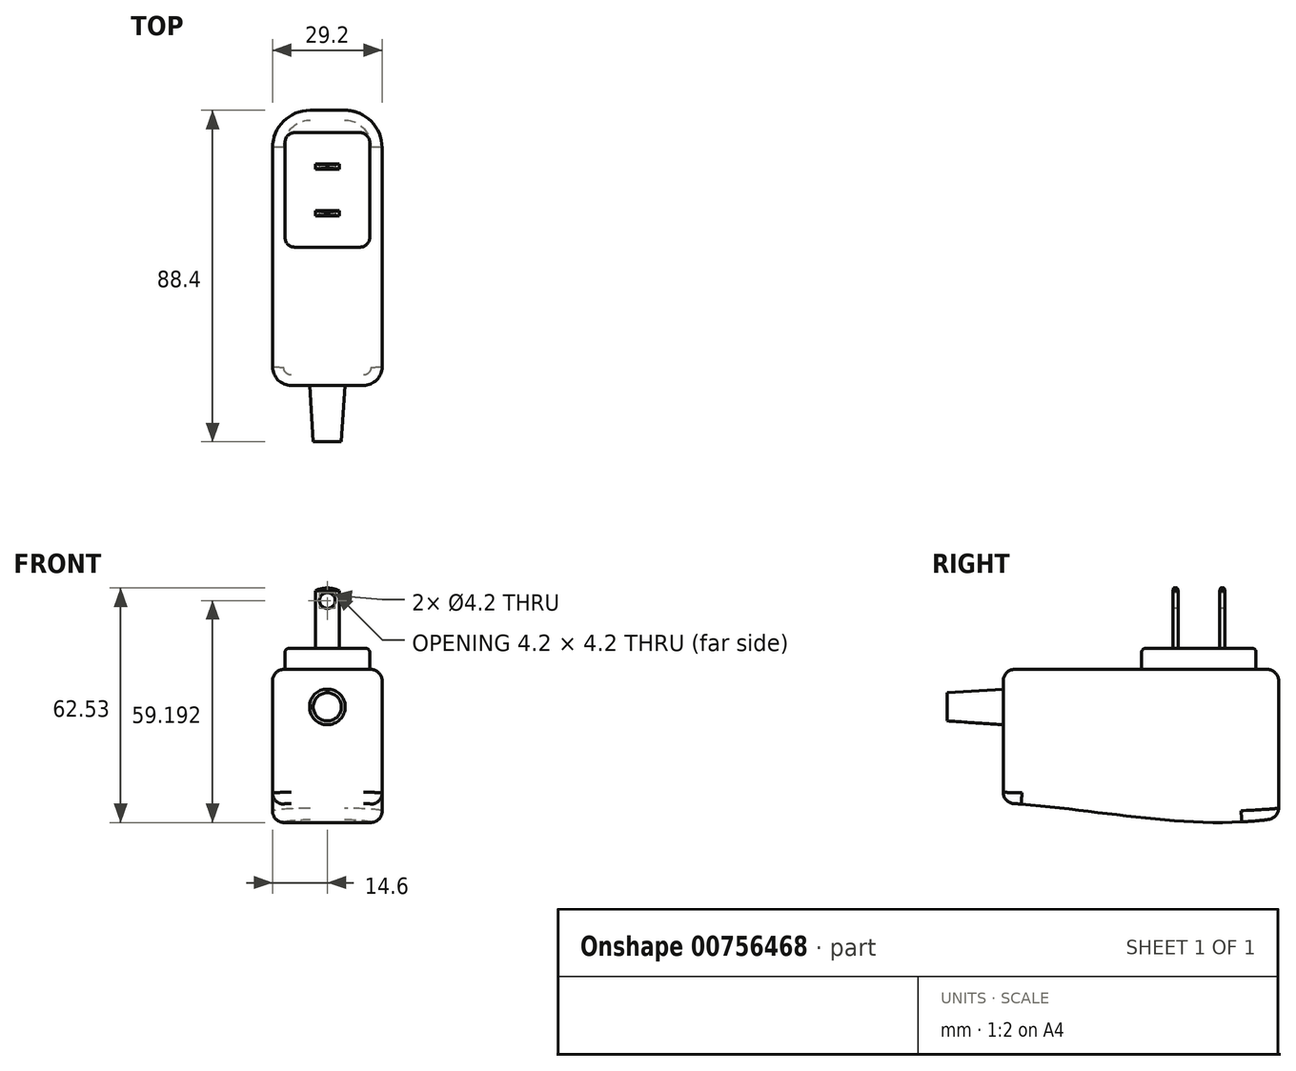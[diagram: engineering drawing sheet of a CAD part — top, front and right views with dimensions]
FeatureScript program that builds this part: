
annotation { "Feature Type Name" : "Feature", "Feature Type Description" : "" }
export const myFeature = defineFeature(function(context is Context, id is Id, definition is map)
    precondition{}
    {
        {
            var Q0;
            Q0=qCreatedBy(makeId("Top.planeOp"),FACE);
            var sketch = newSketch(context, id + "F0", { "sketchPlane" : qUnion([Q0])});
            skLineSegment(sketch, "E0.bottom", {"start": v(-9.6, -36.7) * mm, "end": v(9.6, -36.7) * mm});
            skLineSegment(sketch, "E0.top", {"start": v(-4.6, 36.7) * mm, "end": v(4.6, 36.7) * mm});
            skLineSegment(sketch, "E0.left", {"start": v(-14.6, -31.7) * mm, "end": v(-14.6, 26.7) * mm});
            skLineSegment(sketch, "E0.right", {"start": v(14.6, -31.7) * mm, "end": v(14.6, 26.7) * mm});
            skPoint(sketch, "E0.middle", {"position": v(0, 0) * mm});
            skPoint(sketch, "E1.visualSharp", {"position": v(-14.6, 36.7) * mm});
            skArc(sketch, "E1.filletArc", {"start": v(-4.6, 36.7) * mm, "mid": v(-11.67, 33.77) * mm, "end": v(-14.6, 26.7) * mm});
            skPoint(sketch, "E2.visualSharp", {"position": v(14.6, 36.7) * mm});
            skArc(sketch, "E2.filletArc", {"start": v(14.6, 26.7) * mm, "mid": v(11.67, 33.77) * mm, "end": v(4.6, 36.7) * mm});
            skPoint(sketch, "E3.visualSharp", {"position": v(-14.6, -36.7) * mm});
            skArc(sketch, "E3.filletArc", {"start": v(-14.6, -31.7) * mm, "mid": v(-13.14, -35.24) * mm, "end": v(-9.6, -36.7) * mm});
            skPoint(sketch, "E4.visualSharp", {"position": v(14.6, -36.7) * mm});
            skArc(sketch, "E4.filletArc", {"start": v(9.6, -36.7) * mm, "mid": v(13.14, -35.24) * mm, "end": v(14.6, -31.7) * mm});
            skSolve(sketch);
        }
        {
            var Q0;
            Q0=makeQuery(id+"F0.imprint","IMPRINT",FACE,{"disambiguationData":[TD([[makeQuery(id+"F0.imprint","IMPRINT",EDGE,{"derivedFrom":sQuery(id+"F0.wireOp",EDGE,"E0.bottom")}),1.0]])]});
            extrude(context, id + "F1", {"entities" : qUnion([Q0]), "oppositeDirection" : true, "depth" : 35.6 * mm, "offsetDistance" : 25 * mm});
        }
        {
            var Q0;
            Q0=makeQuery(id+"F1.opExtrude","CAP_FACE",FACE,{"disambiguationData":[OSD([sQuery(id+"F0.wireOp",EDGE,"E0.bottom"),sQuery(id+"F0.wireOp",EDGE,"E0.top"),sQuery(id+"F0.wireOp",EDGE,"E0.left"),sQuery(id+"F0.wireOp",EDGE,"E0.right"),sQuery(id+"F0.wireOp",EDGE,"E1.filletArc"),sQuery(id+"F0.wireOp",EDGE,"E2.filletArc"),sQuery(id+"F0.wireOp",EDGE,"E3.filletArc"),sQuery(id+"F0.wireOp",EDGE,"E4.filletArc")])],"isStart":true});
            var sketch = newSketch(context, id + "F2", { "sketchPlane" : qUnion([Q0])});
            skLineSegment(sketch, "E5", {"start": v(0, 36.7) * mm, "end": v(0, -36.7) * mm, "construction": true});
            skLineSegment(sketch, "E6.bottom", {"start": v(-8.77, 0.2) * mm, "end": v(8.78, 0.2) * mm});
            skLineSegment(sketch, "E6.top", {"start": v(-8.77, 30.7) * mm, "end": v(8.78, 30.7) * mm});
            skLineSegment(sketch, "E6.left", {"start": v(-11.27, 2.7) * mm, "end": v(-11.27, 28.2) * mm});
            skLineSegment(sketch, "E6.right", {"start": v(11.28, 2.7) * mm, "end": v(11.28, 28.2) * mm});
            skPoint(sketch, "E6.middle", {"position": v(0, 15.45) * mm});
            skPoint(sketch, "E7.visualSharp", {"position": v(-11.27, 30.7) * mm});
            skArc(sketch, "E7.filletArc", {"start": v(-8.77, 30.7) * mm, "mid": v(-10.54, 29.97) * mm, "end": v(-11.27, 28.2) * mm});
            skPoint(sketch, "E8.visualSharp", {"position": v(11.28, 30.7) * mm});
            skArc(sketch, "E8.filletArc", {"start": v(11.28, 28.2) * mm, "mid": v(10.54, 29.97) * mm, "end": v(8.78, 30.7) * mm});
            skPoint(sketch, "E9.visualSharp", {"position": v(11.28, 0.2) * mm});
            skArc(sketch, "E9.filletArc", {"start": v(8.78, 0.2) * mm, "mid": v(10.54, 0.93) * mm, "end": v(11.28, 2.7) * mm});
            skPoint(sketch, "E10.visualSharp", {"position": v(-11.27, 0.2) * mm});
            skArc(sketch, "E10.filletArc", {"start": v(-11.27, 2.7) * mm, "mid": v(-10.54, 0.93) * mm, "end": v(-8.77, 0.2) * mm});
            skSolve(sketch);
        }
        {
            var Q0;
            Q0=makeQuery(id+"F2.imprint","IMPRINT",FACE,{"disambiguationData":[TD([[makeQuery(id+"F2.imprint","IMPRINT",EDGE,{"derivedFrom":sQuery(id+"F2.wireOp",EDGE,"E6.bottom")}),1.0]])]});
            extrude(context, id + "F3", {"entities" : qUnion([Q0]), "operationType" : NewBodyOperationType.ADD, "depth" : 5.6 * mm, "offsetDistance" : 25 * mm});
        }
        {
            var Q0;
            Q0=makeQuery(id+"F3.opExtrude","CAP_FACE",FACE,{"disambiguationData":[OSD([sQuery(id+"F2.wireOp",EDGE,"E6.bottom"),sQuery(id+"F2.wireOp",EDGE,"E6.top"),sQuery(id+"F2.wireOp",EDGE,"E6.left"),sQuery(id+"F2.wireOp",EDGE,"E6.right"),sQuery(id+"F2.wireOp",EDGE,"E7.filletArc"),sQuery(id+"F2.wireOp",EDGE,"E8.filletArc"),sQuery(id+"F2.wireOp",EDGE,"E9.filletArc"),sQuery(id+"F2.wireOp",EDGE,"E10.filletArc")])],"isStart":false});
            var sketch = newSketch(context, id + "F4", { "sketchPlane" : qUnion([Q0])});
            skLineSegment(sketch, "E11", {"start": v(0, 30.7) * mm, "end": v(0, 0) * mm, "construction": true});
            skLineSegment(sketch, "E12", {"start": v(-3.12, 9.9) * mm, "end": v(3.13, 9.9) * mm});
            skLineSegment(sketch, "E13", {"start": v(-3.13, 21) * mm, "end": v(3.13, 21) * mm});
            skLineSegment(sketch, "E14.0", {"start": v(-8.77, 0.2) * mm, "end": v(8.78, 0.2) * mm, "construction": true});
            skLineSegment(sketch, "E14.1", {"start": v(-8.77, 30.7) * mm, "end": v(8.78, 30.7) * mm, "construction": true});
            skLineSegment(sketch, "E15", {"start": v(-3.12, 8.5) * mm, "end": v(3.13, 8.5) * mm});
            skLineSegment(sketch, "E16", {"start": v(3.13, 22.4) * mm, "end": v(-3.13, 22.4) * mm});
            skLineSegment(sketch, "E17", {"start": v(-3.13, 22.4) * mm, "end": v(-3.13, 21) * mm});
            skLineSegment(sketch, "E18.MirrorCS", {"start": v(3.13, 22.4) * mm, "end": v(3.13, 21) * mm});
            skLineSegment(sketch, "E19.trimOffspring", {"start": v(-3.12, 9.9) * mm, "end": v(-3.12, 8.5) * mm});
            skLineSegment(sketch, "E20.trimOffspring", {"start": v(3.13, 9.9) * mm, "end": v(3.13, 8.5) * mm});
            skSolve(sketch);
        }
        {
            var Q0;
            Q0=makeQuery(id+"F4.imprint","IMPRINT",FACE,{"disambiguationData":[TD([[makeQuery(id+"F4.imprint","IMPRINT",EDGE,{"derivedFrom":sQuery(id+"F4.wireOp",EDGE,"E13")}),1.0]])]});
            var Q1;
            Q1=makeQuery(id+"F4.imprint","IMPRINT",FACE,{"disambiguationData":[TD([[makeQuery(id+"F4.imprint","IMPRINT",EDGE,{"derivedFrom":sQuery(id+"F4.wireOp",EDGE,"E12")}),-1.0]])]});
            extrude(context, id + "F5", {"entities" : qUnion([Q0, Q1]), "operationType" : NewBodyOperationType.ADD, "depth" : 16.1 * mm, "offsetDistance" : 25 * mm});
        }
        {
            var Q0;
            Q0=makeQuery(id+"F1.opExtrude","SWEPT_FACE",FACE,{"disambiguationData":[OSD([sQuery(id+"F0.wireOp",EDGE,"E0.left")])]});
            var sketch = newSketch(context, id + "F6", { "sketchPlane" : qUnion([Q0])});
            skLineSegment(sketch, "E21.0", {"start": v(31.7, -35.6) * mm, "end": v(-26.7, -35.6) * mm});
            skPoint(sketch, "E21.1", {"position": v(36.7, -35.6) * mm});
            skPoint(sketch, "E22.0", {"position": v(-36.7, -35.6) * mm});
            skLineSegment(sketch, "E23", {"start": v(-36.7, -35.6) * mm, "end": v(-26.7, -35.6) * mm});
            skLineSegment(sketch, "E24", {"start": v(36.7, -35.6) * mm, "end": v(31.7, -35.6) * mm});
            skLineSegment(sketch, "E25", {"start": v(-36.7, -35.6) * mm, "end": v(-36.7, -39.6) * mm});
            skFitSpline(sketch, "E26", {"points": [v(-36.7, -39.6) * mm, v(36.7, -35.6) * mm], "startDerivative": vector(68.4, -11.78) * mm, "endDerivative": vector(73.4, 4) * mm});
            skSolve(sketch);
        }
        {
            var Q0;
            Q0=makeQuery(id+"F6.imprint","IMPRINT",FACE,{"disambiguationData":[TD([[makeQuery(id+"F6.imprint","IMPRINT",EDGE,{"derivedFrom":sQuery(id+"F6.wireOp",EDGE,"E21.0")}),1.0]])]});
            var Q1;
            Q1=makeQuery(id+"F1.opExtrude","SWEPT_FACE",FACE,{"disambiguationData":[OSD([sQuery(id+"F0.wireOp",EDGE,"E0.right")])]});
            extrude(context, id + "F7", {"entities" : qUnion([Q0]), "operationType" : NewBodyOperationType.ADD, "endBound" : BoundingType.UP_TO_SURFACE, "oppositeDirection" : true, "depth" : 25 * mm, "endBoundEntityFace" : qUnion([Q1]), "offsetDistance" : 25 * mm});
        }
        {
            var Q0;
            {var subQ1=sQuery(id+"F6.wireOp",EDGE,"E24");var subQ2=sQuery(id+"F6.wireOp",EDGE,"E23");var subQ3=sQuery(id+"F6.wireOp",EDGE,"E21.0");Q0=makeQuery(id+"F7.boolean.opBoolean","SPLIT",FACE,{"disambiguationData":[TD([makeQuery(id+"F1.opExtrude","SWEPT_FACE",FACE,{"disambiguationData":[OSD([sQuery(id+"F0.wireOp",EDGE,"E1.filletArc")])]})])],"derivedFrom":makeQuery(id+"F7.opExtrude","SWEPT_FACE",FACE,{"disambiguationData":[OSD([subQ3,subQ2,subQ1])]})});}
            var Q1;
            {var subQ1=sQuery(id+"F6.wireOp",EDGE,"E24");var subQ2=sQuery(id+"F6.wireOp",EDGE,"E23");var subQ3=sQuery(id+"F6.wireOp",EDGE,"E21.0");Q1=makeQuery(id+"F7.boolean.opBoolean","SPLIT",FACE,{"disambiguationData":[TD([makeQuery(id+"F1.opExtrude","SWEPT_FACE",FACE,{"disambiguationData":[OSD([sQuery(id+"F0.wireOp",EDGE,"E2.filletArc")])]})])],"derivedFrom":makeQuery(id+"F7.opExtrude","SWEPT_FACE",FACE,{"disambiguationData":[OSD([subQ3,subQ2,subQ1])]})});}
            var Q2;
            {var subQ1=sQuery(id+"F6.wireOp",EDGE,"E24");var subQ2=sQuery(id+"F6.wireOp",EDGE,"E23");var subQ3=sQuery(id+"F6.wireOp",EDGE,"E21.0");Q2=makeQuery(id+"F7.boolean.opBoolean","SPLIT",FACE,{"disambiguationData":[TD([makeQuery(id+"F1.opExtrude","SWEPT_FACE",FACE,{"disambiguationData":[OSD([sQuery(id+"F0.wireOp",EDGE,"E3.filletArc")])]})])],"derivedFrom":makeQuery(id+"F7.opExtrude","SWEPT_FACE",FACE,{"disambiguationData":[OSD([subQ3,subQ2,subQ1])]})});}
            var Q3;
            {var subQ1=sQuery(id+"F6.wireOp",EDGE,"E24");var subQ2=sQuery(id+"F6.wireOp",EDGE,"E23");var subQ3=sQuery(id+"F6.wireOp",EDGE,"E21.0");Q3=makeQuery(id+"F7.boolean.opBoolean","SPLIT",FACE,{"disambiguationData":[TD([makeQuery(id+"F1.opExtrude","SWEPT_FACE",FACE,{"disambiguationData":[OSD([sQuery(id+"F0.wireOp",EDGE,"E4.filletArc")])]})])],"derivedFrom":makeQuery(id+"F7.opExtrude","SWEPT_FACE",FACE,{"disambiguationData":[OSD([subQ3,subQ2,subQ1])]})});}
            extrude(context, id + "F8", {"entities" : qUnion([Q0, Q1, Q2, Q3]), "operationType" : NewBodyOperationType.REMOVE, "oppositeDirection" : true, "depth" : 6 * mm, "offsetDistance" : 25 * mm});
        }
        {
            var Q0;
            Q0=makeQuery(id+"F5.opExtrude","SWEPT_FACE",FACE,{"disambiguationData":[OSD([sQuery(id+"F4.wireOp",EDGE,"E15")])]});
            var sketch = newSketch(context, id + "F9", { "sketchPlane" : qUnion([Q0])});
            skLineSegment(sketch, "E27", {"start": v(0, 21.7) * mm, "end": v(0, 5.6) * mm, "construction": true});
            skCircle(sketch, "E28", {"center": v(0, 18.36) * mm, "radius": 2.1 * mm});
            skLineSegment(sketch, "E29", {"start": v(-3.12, 20.99) * mm, "end": v(3.13, 20.99) * mm, "construction": true});
            skArc(sketch, "E30", {"start": v(3.13, 20.99) * mm, "mid": v(0, 21.7) * mm, "end": v(-3.12, 20.99) * mm});
            skLineSegment(sketch, "E31.0", {"start": v(-3.12, 21.7) * mm, "end": v(-3.12, 5.6) * mm});
            skLineSegment(sketch, "E31.1", {"start": v(-3.12, 21.7) * mm, "end": v(3.13, 21.7) * mm});
            skLineSegment(sketch, "E31.2", {"start": v(3.13, 21.7) * mm, "end": v(3.13, 5.6) * mm});
            skSolve(sketch);
        }
        {
            var Q0;
            Q0=makeQuery(id+"F9.imprint","IMPRINT",FACE,{"disambiguationData":[TD([[makeQuery(id+"F9.imprint","IMPRINT",EDGE,{"derivedFrom":sQuery(id+"F9.wireOp",EDGE,"E28")}),1.0]])]});
            var Q1;
            {var subQ0=sQuery(id+"F9.wireOp",EDGE,"E31.0");var subQ1=sQuery(id+"F9.wireOp",EDGE,"E30");var subQ2=makeQuery(id+"F9.imprint","INTERSECT",VERTEX,{"derivedFrom":[subQ1,subQ0]});Q1=makeQuery(id+"F9.imprint","IMPRINT",FACE,{"disambiguationData":[TD([[makeQuery(id+"F9.imprint","IMPRINT",EDGE,{"disambiguationData":[TD([[subQ2,1.0]])],"derivedFrom":subQ1}),-1.0]])]});}
            var Q2;
            {var subQ0=sQuery(id+"F9.wireOp",EDGE,"E31.2");var subQ1=sQuery(id+"F9.wireOp",EDGE,"E30");var subQ2=makeQuery(id+"F9.imprint","INTERSECT",VERTEX,{"derivedFrom":[subQ1,subQ0]});Q2=makeQuery(id+"F9.imprint","IMPRINT",FACE,{"disambiguationData":[TD([[makeQuery(id+"F9.imprint","IMPRINT",EDGE,{"disambiguationData":[TD([[subQ2,-1.0]])],"derivedFrom":subQ1}),-1.0]])]});}
            extrude(context, id + "F10", {"entities" : qUnion([Q0, Q1, Q2]), "operationType" : NewBodyOperationType.REMOVE, "oppositeDirection" : true, "depth" : 25 * mm, "offsetDistance" : 25 * mm});
        }
        {
            var Q0;
            Q0=makeQuery(id+"F5.opExtrude","SWEPT_FACE",FACE,{"disambiguationData":[OSD([sQuery(id+"F4.wireOp",EDGE,"E20.trimOffspring")])]});
            var sketch = newSketch(context, id + "F11", { "sketchPlane" : qUnion([Q0])});
            skLineSegment(sketch, "E32.0", {"start": v(8.5, 20.99) * mm, "end": v(8.5, 21.7) * mm});
            skLineSegment(sketch, "E32.1", {"start": v(9.9, 20.99) * mm, "end": v(9.9, 21.7) * mm});
            skLineSegment(sketch, "E32.2", {"start": v(21, 20.99) * mm, "end": v(21, 21.7) * mm});
            skLineSegment(sketch, "E32.3", {"start": v(22.4, 20.99) * mm, "end": v(22.4, 21.7) * mm});
            skLineSegment(sketch, "E33", {"start": v(8.5, 21.7) * mm, "end": v(9.9, 21.7) * mm});
            skLineSegment(sketch, "E34", {"start": v(21, 21.7) * mm, "end": v(22.4, 21.7) * mm});
            skLineSegment(sketch, "E35", {"start": v(8.5, 20.99) * mm, "end": v(8.73, 21.7) * mm});
            skLineSegment(sketch, "E36", {"start": v(9.9, 20.99) * mm, "end": v(9.67, 21.7) * mm});
            skLineSegment(sketch, "E37", {"start": v(21, 20.99) * mm, "end": v(21.23, 21.7) * mm});
            skLineSegment(sketch, "E38", {"start": v(22.4, 20.99) * mm, "end": v(22.17, 21.7) * mm});
            skSolve(sketch);
        }
        {
            var Q0;
            {var subQ0=sQuery(id+"F11.wireOp",EDGE,"E32.0");Q0=makeQuery(id+"F11.imprint","IMPRINT",FACE,{"disambiguationData":[TD([[makeQuery(id+"F11.imprint","IMPRINT",EDGE,{"derivedFrom":subQ0}),-1.0]])]});}
            var Q1;
            {var subQ0=sQuery(id+"F11.wireOp",EDGE,"E32.1");Q1=makeQuery(id+"F11.imprint","IMPRINT",FACE,{"disambiguationData":[TD([[makeQuery(id+"F11.imprint","IMPRINT",EDGE,{"derivedFrom":subQ0}),1.0]])]});}
            var Q2;
            {var subQ0=sQuery(id+"F11.wireOp",EDGE,"E32.2");Q2=makeQuery(id+"F11.imprint","IMPRINT",FACE,{"disambiguationData":[TD([[makeQuery(id+"F11.imprint","IMPRINT",EDGE,{"derivedFrom":subQ0}),-1.0]])]});}
            var Q3;
            {var subQ0=sQuery(id+"F11.wireOp",EDGE,"E32.3");Q3=makeQuery(id+"F11.imprint","IMPRINT",FACE,{"disambiguationData":[TD([[makeQuery(id+"F11.imprint","IMPRINT",EDGE,{"derivedFrom":subQ0}),1.0]])]});}
            extrude(context, id + "F12", {"entities" : qUnion([Q0, Q1, Q2, Q3]), "operationType" : NewBodyOperationType.REMOVE, "oppositeDirection" : true, "depth" : 25 * mm, "offsetDistance" : 25 * mm});
        }
        {
            var Q0;
            Q0=makeQuery(id+"F1.opExtrude","CAP_EDGE",EDGE,{"disambiguationData":[OSD([sQuery(id+"F0.wireOp",EDGE,"E0.right")])],"isStart":true});
            fillet(context, id + "F13", {"entities" : qUnion([Q0]), "radius" : 3 * mm, "tangentPropagation" : true, "allowEdgeOverflow" : false});
        }
        {
            var Q0;
            Q0=makeQuery(id+"F3.opExtrude","CAP_EDGE",EDGE,{"disambiguationData":[OSD([sQuery(id+"F2.wireOp",EDGE,"E6.right")])],"isStart":false});
            fillet(context, id + "F14", {"entities" : qUnion([Q0]), "radius" : 1 * mm, "tangentPropagation" : true, "allowEdgeOverflow" : false});
        }
        {
            var Q0;
            Q0=makeQuery(id+"F7.opExtrude","CAP_EDGE",EDGE,{"disambiguationData":[OSD([sQuery(id+"F6.wireOp",EDGE,"E26")])],"isStart":false});
            fillet(context, id + "F15", {"entities" : qUnion([Q0]), "radius" : 3 * mm, "tangentPropagation" : true, "allowEdgeOverflow" : false});
        }
        {
            var Q0;
            Q0=makeQuery(id+"F1.opExtrude","SWEPT_FACE",FACE,{"disambiguationData":[OSD([sQuery(id+"F0.wireOp",EDGE,"E0.bottom")])]});
            var sketch = newSketch(context, id + "F16", { "sketchPlane" : qUnion([Q0])});
            skLineSegment(sketch, "E39.0", {"start": v(9.6, -3) * mm, "end": v(-9.6, -3) * mm, "construction": true});
            skCircle(sketch, "E40", {"center": v(0, -10) * mm, "radius": 4.75 * mm});
            skPoint(sketch, "E40.centerSnap0", {"position": v(0, -3) * mm});
            skSolve(sketch);
        }
        {
            var Q0;
            Q0=makeQuery(id+"F16.imprint","IMPRINT",FACE,{"disambiguationData":[TD([[makeQuery(id+"F16.imprint","IMPRINT",EDGE,{"derivedFrom":sQuery(id+"F16.wireOp",EDGE,"E40")}),-1.0]])]});
            cPlane(context, id + "F17", {"entities" : qUnion([Q0]), "cplaneType" : CPlaneType.OFFSET, "offset" : 15 * mm, "width" : 150 * mm, "height" : 150 * mm});
        }
        {
            var Q0;
            Q0=qCreatedBy(id+"F17.planeOp",FACE);
            var sketch = newSketch(context, id + "F18", { "sketchPlane" : qUnion([Q0])});
            skCircle(sketch, "E41.0", {"center": v(0, -10) * mm, "radius": 4.75 * mm, "construction": true});
            skCircle(sketch, "E42", {"center": v(0, -10) * mm, "radius": 3.75 * mm});
            skSolve(sketch);
        }
        {
            var Q0;
            Q0=sQuery(id+"F18.wireOp",VERTEX,"E41.0.center");
            var Q1;
            Q1=qCreatedBy(makeId("Top.planeOp"),FACE);
            cPlane(context, id + "F19", {"entities" : qUnion([Q0, Q1]), "cplaneType" : CPlaneType.PLANE_POINT, "offset" : 25 * mm, "width" : 150 * mm, "height" : 150 * mm});
        }
        {
            var Q1;
            Q1=makeQuery(id+"F16.imprint","IMPRINT",FACE,{"disambiguationData":[TD([[makeQuery(id+"F16.imprint","IMPRINT",EDGE,{"derivedFrom":sQuery(id+"F16.wireOp",EDGE,"E40")}),1.0]])]});
            var Q2;
            Q2=makeQuery(id+"F18.imprint","IMPRINT",FACE,{"disambiguationData":[TD([[makeQuery(id+"F18.imprint","IMPRINT",EDGE,{"derivedFrom":sQuery(id+"F18.wireOp",EDGE,"E42")}),1.0]])]});
            loft(context, id + "F20", {"operationType" : NewBodyOperationType.ADD, "sheetProfilesArray" : [{ "sheetProfileEntities" : qUnion([Q1]) }, { "sheetProfileEntities" : qUnion([Q2]) }]});
        }
    });
